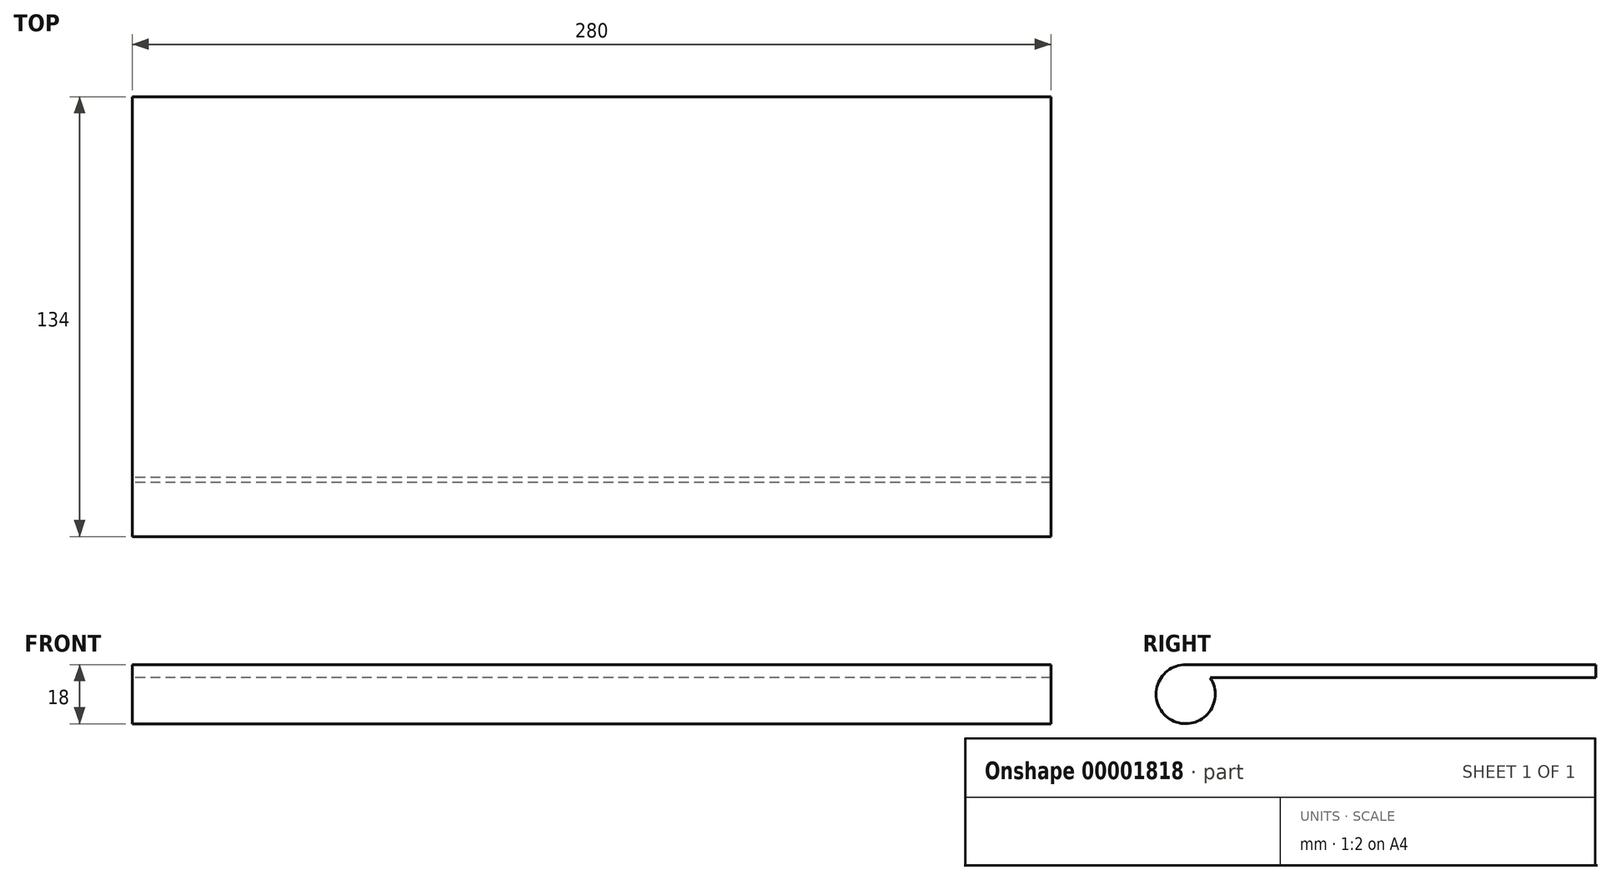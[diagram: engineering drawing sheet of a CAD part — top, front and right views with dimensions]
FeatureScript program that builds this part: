
annotation { "Feature Type Name" : "Feature", "Feature Type Description" : "" }
export const myFeature = defineFeature(function(context is Context, id is Id, definition is map)
    precondition{}
    {
        {
            var Q0;
            Q0=qCreatedBy(makeId("Right.planeOp"),FACE);
            var sketch = newSketch(context, id + "F0", { "sketchPlane" : qUnion([Q0])});
            skArc(sketch, "E0", {"start": v(0, 9) * mm, "mid": v(-4.24, -7.94) * mm, "end": v(7.48, 5) * mm});
            skLineSegment(sketch, "E1", {"start": v(0, 9) * mm, "end": v(125, 9) * mm});
            skLineSegment(sketch, "E2", {"start": v(125, 9) * mm, "end": v(125, 5) * mm});
            skLineSegment(sketch, "E3", {"start": v(125, 5) * mm, "end": v(7.48, 5) * mm});
            skSolve(sketch);
        }
        {
            var Q0;
            Q0 = qSketchRegion(id + "F0", true);
            extrude(context, id + "F1", {"entities" : qUnion([Q0]), "depth" : 280 * mm});
        }
    });
